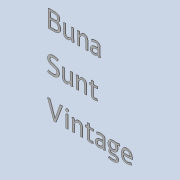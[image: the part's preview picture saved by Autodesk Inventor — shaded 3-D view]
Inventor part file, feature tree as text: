
AUTODESK INVENTOR PART (.ipt)
format: ipt  version: 2020 (Build 240168000, 168)  size: 640,000 bytes
history: native  units: mm
features: extrude x1, sketch x1
ambient origin geometry x8: Origin, YZ Plane, XZ Plane, XY Plane, X Axis, Y Axis, Z Axis, Center Point
bodies: Solid1 (feature_tree)
feature tree (2):
  extrude  "Extrusion1"  Depth=200.0mm
  sketch  "Sketch1"  dims[d0=300.0mm d1=200.0mm d2=0.6mm d3=0.0mm]
